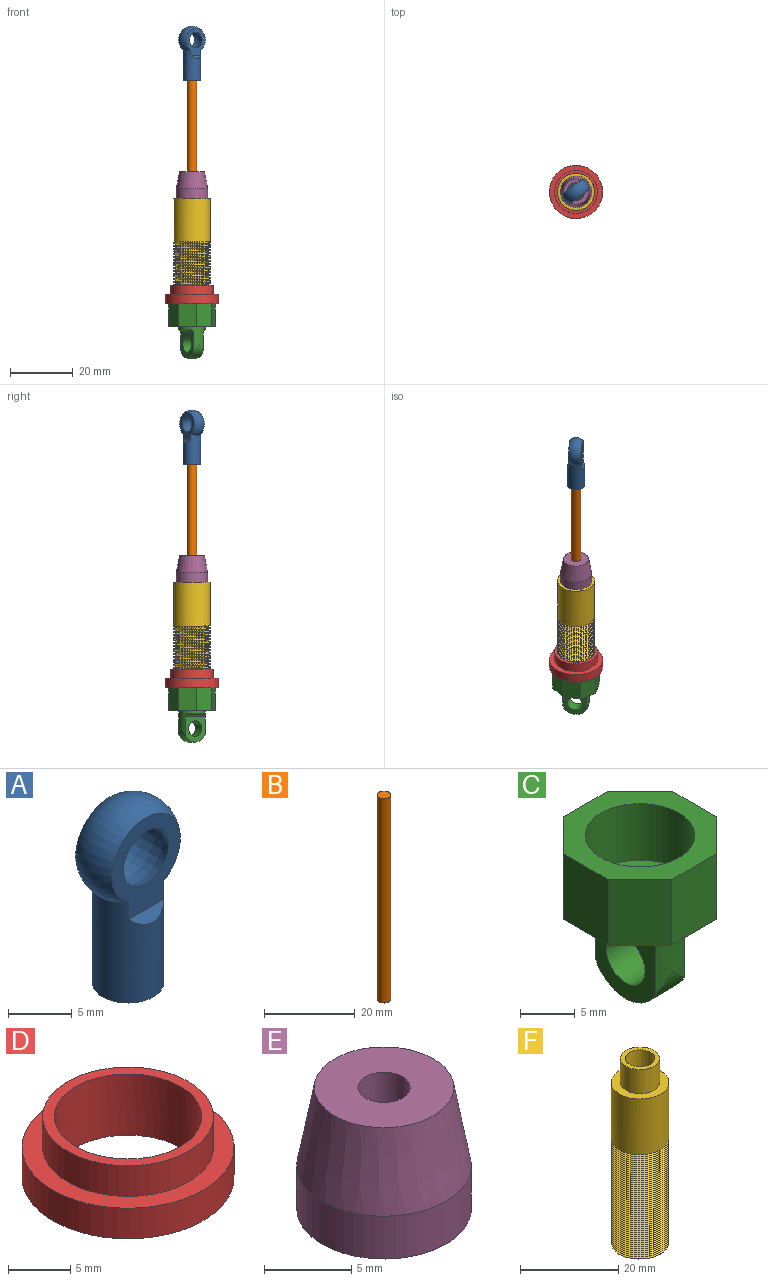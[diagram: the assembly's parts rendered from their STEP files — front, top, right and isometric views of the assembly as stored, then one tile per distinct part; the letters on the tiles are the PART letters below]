
ASSEMBLY  parts=6 mates=9
PART A: 10 faces, bbox 7.6x5.6x16.8 mm
  f0: cylinder r=2.8mm len=9.75mm, axis (0,0,1), area 150.2mm2, adj f1,f2,f3,f5,f8,f9
  f1: plane 8.79x7.59mm, normal (0,-1,0), area 31mm2, adj f0,f2,f4,f8
  f2: torus R=1.32mm, axis (0,1,0), area 92.4mm2, adj f0,f1,f3
  f3: plane 8.79x7.59mm, normal (0,1,0), area 31mm2, adj f0,f2,f4,f9
  f4: revolved ~6x6mm, area 74.1mm2, adj f1,f3
  f5: plane 5.6x5.6mm, normal (0,0,-1), area 17.6mm2, adj f0,f7
  f6: torus R=1.32mm, axis (0,1,0), area 7.4mm2, adj f7
  f7: cylinder r=1.5mm len=8.88mm, axis (0,0,-1), area 83.1mm2, adj f5,f6
  f8: plane 3.92x0.8mm, normal (0,-0.71,0.71), area 3.1mm2, adj f0,f1
  f9: plane 3.92x0.8mm, normal (0,0.71,0.71), area 3.1mm2, adj f0,f3
PART B: 3 faces, bbox 3x3x55 mm
  f0: cylinder r=1.5mm len=55mm, axis (0,0,-1), area 518.4mm2, adj f1,f2
  f1: plane 3x3mm, normal (0,0,1), area 7.1mm2, adj f0
  f2: plane 3x3mm, normal (0,0,-1), area 7.1mm2, adj f0
PART C: 21 faces, bbox 14x14x17.3 mm
  f0: cylinder r=4.25mm len=8.5mm, axis (0,0,1), area 71.3mm2, adj f1,f2,f12,f15,f16,f18,f19,f20
  f1: plane 8x7.65mm, normal (1,0,0), area 36.4mm2, adj f0,f17,f18,f19
  f2: plane 8x7.65mm, normal (-1,0,0), area 36.4mm2, adj f0,f17,f18,f20
  f3: plane 7.3x5.8mm, normal (0,-1,0), area 42.3mm2, adj f4,f10,f11,f12
  f4: plane 7.3x4.1mm, normal (0.71,-0.71,0), area 42.3mm2, adj f3,f5,f11,f12
  f5: plane 7.3x5.8mm, normal (1,0,0), area 42.3mm2, adj f4,f6,f11,f12
  f6: plane 7.3x4.1mm, normal (0.71,0.71,0), area 42.3mm2, adj f5,f7,f11,f12
  f7: plane 7.3x5.8mm, normal (0,1,0), area 42.3mm2, adj f6,f8,f11,f12
  f8: plane 7.3x4.1mm, normal (-0.71,0.71,0), area 42.3mm2, adj f7,f9,f11,f12
  f9: plane 7.3x5.8mm, normal (-1,0,0), area 42.3mm2, adj f8,f10,f11,f12
  f10: plane 7.3x4.1mm, normal (-0.71,-0.71,0), area 42.3mm2, adj f3,f9,f11,f12
  f11: plane 14x14mm, normal (0,0,1), area 83.8mm2, adj f3,f4,f5,f6,f7,f8,f9,f10
  f12: plane 14x14mm, normal (0,0,-1), area 105.6mm2, adj f0,f3,f4,f5,f6,f7,f8,f9
  f13: cylinder r=5mm len=10mm, axis (0,0,1), area 197.9mm2, adj f11,f14
  f14: plane 10x10mm, normal (0,0,1), area 78.5mm2, adj f13
  f15: plane 6.31x1.4mm, normal (0,0,-1), area 6.1mm2, adj f0,f19
  f16: plane 6.31x1.4mm, normal (0,0,-1), area 6.1mm2, adj f0,f20
  f17: cylinder r=2.5mm len=5mm, axis (-1,0,0), area 58.1mm2, adj f1,f2
  f18: cylinder r=4.25mm len=8.5mm, axis (-1,0,0), area 42.4mm2, adj f0,f1,f2
  f19: cylinder r=1mm len=7.65mm, axis (0,1,0), area 11.3mm2, adj f0,f1,f15
  f20: cylinder r=1mm len=7.65mm, axis (0,-1,0), area 11.3mm2, adj f0,f2,f16
PART D: 6 faces, bbox 17x17x6 mm
  f0: cylinder r=8.5mm len=17mm, axis (0,0,-1), area 160.2mm2, adj f1,f2
  f1: plane 17x17mm, normal (0,0,1), area 79.6mm2, adj f0,f3
  f2: plane 17x17mm, normal (0,0,-1), area 117.6mm2, adj f0,f5
  f3: cylinder r=6.85mm len=13.7mm, axis (0,0,-1), area 129.1mm2, adj f1,f4
  f4: plane 13.7x13.7mm, normal (0,0,1), area 38.1mm2, adj f3,f5
  f5: cylinder r=5.9mm len=11.8mm, axis (0,0,-1), area 222.4mm2, adj f2,f4
PART E: 7 faces, bbox 10x10x8.5 mm
  f0: cylinder r=5mm len=10mm, axis (0,0,-1), area 94.2mm2, adj f1,f3
  f1: plane 10x10mm, normal (0,0,-1), area 28.3mm2, adj f0,f4
  f2: plane 8x8mm, normal (0,0,1), area 43.2mm2, adj f3,f6
  f3: cone r=5mm half-angle=10.3deg, axis (0,0,-1), area 158.1mm2, adj f0,f2
  f4: cylinder r=4mm len=8mm, axis (0,0,-1), area 150.8mm2, adj f1,f5
  f5: plane 8x8mm, normal (0,0,-1), area 43.2mm2, adj f4,f6
  f6: cylinder r=1.5mm len=3mm, axis (0,0,-1), area 23.6mm2, adj f2,f5
PART F: 66 faces, bbox 12.2x14.1x46.7 mm
  f0: cylinder r=5.9mm len=14.26mm, axis (0,0,-1), area 519.2mm2, adj f52,f53,f63,f64
  f1: cylinder r=5.9mm len=11.8mm, axis (0,0,-1), area 0.2mm2, adj f2,f54,f62,f65
  f2: cylinder r=5.9mm len=11.8mm, axis (0,0,-1), area 0.5mm2, adj f1,f3,f62,f64
  f3: cylinder r=5.9mm len=11.8mm, axis (0,0,-1), area 0.5mm2, adj f2,f4,f62,f64
  f4: cylinder r=5.9mm len=11.8mm, axis (0,0,-1), area 0.5mm2, adj f3,f5,f62,f64
  f5: cylinder r=5.9mm len=11.8mm, axis (0,0,-1), area 0.5mm2, adj f4,f6,f62,f64
  f6: cylinder r=5.9mm len=11.8mm, axis (0,0,-1), area 0.5mm2, adj f5,f7,f62,f64
  f7: cylinder r=5.9mm len=11.8mm, axis (0,0,-1), area 0.5mm2, adj f6,f8,f62,f64
  f8: cylinder r=5.9mm len=11.8mm, axis (0,0,-1), area 0.5mm2, adj f7,f9,f62,f64
  f9: cylinder r=5.9mm len=11.8mm, axis (0,0,-1), area 0.5mm2, adj f8,f10,f62,f64
  f10: cylinder r=5.9mm len=11.8mm, axis (0,0,-1), area 0.5mm2, adj f9,f11,f62,f64
  f11: cylinder r=5.9mm len=11.8mm, axis (0,0,-1), area 0.5mm2, adj f10,f12,f62,f64
  f12: cylinder r=5.9mm len=11.8mm, axis (0,0,-1), area 0.5mm2, adj f11,f13,f62,f64
  f13: cylinder r=5.9mm len=11.8mm, axis (0,0,-1), area 0.5mm2, adj f12,f14,f62,f64
  f14: cylinder r=5.9mm len=11.8mm, axis (0,0,-1), area 0.5mm2, adj f13,f15,f62,f64
  f15: cylinder r=5.9mm len=11.8mm, axis (0,0,-1), area 0.5mm2, adj f14,f16,f62,f64
  f16: cylinder r=5.9mm len=11.8mm, axis (0,0,-1), area 0.5mm2, adj f15,f17,f62,f64
  f17: cylinder r=5.9mm len=11.8mm, axis (0,0,-1), area 0.5mm2, adj f16,f18,f62,f64
  f18: cylinder r=5.9mm len=11.8mm, axis (0,0,-1), area 0.5mm2, adj f17,f19,f62,f64
  f19: cylinder r=5.9mm len=11.8mm, axis (0,0,-1), area 0.5mm2, adj f18,f20,f62,f64
  f20: cylinder r=5.9mm len=11.8mm, axis (0,0,-1), area 0.5mm2, adj f19,f21,f62,f64
  f21: cylinder r=5.9mm len=11.8mm, axis (0,0,-1), area 0.5mm2, adj f20,f22,f62,f64
  f22: cylinder r=5.9mm len=11.8mm, axis (0,0,-1), area 0.5mm2, adj f21,f23,f62,f64
  f23: cylinder r=5.9mm len=11.8mm, axis (0,0,-1), area 0.5mm2, adj f22,f24,f62,f64
  f24: cylinder r=5.9mm len=11.8mm, axis (0,0,-1), area 0.5mm2, adj f23,f25,f62,f64
  f25: cylinder r=5.9mm len=11.8mm, axis (0,0,-1), area 0.5mm2, adj f24,f26,f62,f64
  f26: cylinder r=5.9mm len=11.8mm, axis (0,0,-1), area 0.5mm2, adj f25,f27,f62,f64
  f27: cylinder r=5.9mm len=11.8mm, axis (0,0,-1), area 0.5mm2, adj f26,f28,f62,f64
  f28: cylinder r=5.9mm len=11.8mm, axis (0,0,-1), area 0.5mm2, adj f27,f29,f62,f64
  f29: cylinder r=5.9mm len=11.8mm, axis (0,0,-1), area 0.5mm2, adj f28,f30,f62,f64
  f30: cylinder r=5.9mm len=11.8mm, axis (0,0,-1), area 0.5mm2, adj f29,f31,f62,f64
  f31: cylinder r=5.9mm len=11.8mm, axis (0,0,-1), area 0.5mm2, adj f30,f32,f62,f64
  f32: cylinder r=5.9mm len=11.8mm, axis (0,0,-1), area 0.5mm2, adj f31,f33,f62,f64
  f33: cylinder r=5.9mm len=11.8mm, axis (0,0,-1), area 0.5mm2, adj f32,f34,f62,f64
  f34: cylinder r=5.9mm len=11.8mm, axis (0,0,-1), area 0.5mm2, adj f33,f35,f62,f64
  f35: cylinder r=5.9mm len=11.8mm, axis (0,0,-1), area 0.5mm2, adj f34,f36,f62,f64
  f36: cylinder r=5.9mm len=11.8mm, axis (0,0,-1), area 0.5mm2, adj f35,f37,f62,f64
  f37: cylinder r=5.9mm len=11.8mm, axis (0,0,-1), area 0.5mm2, adj f36,f38,f62,f64
  f38: cylinder r=5.9mm len=11.8mm, axis (0,0,-1), area 0.5mm2, adj f37,f39,f62,f64
  f39: cylinder r=5.9mm len=11.8mm, axis (0,0,-1), area 0.5mm2, adj f38,f40,f62,f64
  f40: cylinder r=5.9mm len=11.8mm, axis (0,0,-1), area 0.5mm2, adj f39,f41,f62,f64
  f41: cylinder r=5.9mm len=11.8mm, axis (0,0,-1), area 0.5mm2, adj f40,f42,f62,f64
  f42: cylinder r=5.9mm len=11.8mm, axis (0,0,-1), area 0.5mm2, adj f41,f43,f62,f64
  f43: cylinder r=5.9mm len=11.8mm, axis (0,0,-1), area 0.5mm2, adj f42,f44,f62,f64
  f44: cylinder r=5.9mm len=11.8mm, axis (0,0,-1), area 0.5mm2, adj f43,f45,f62,f64
  f45: cylinder r=5.9mm len=11.8mm, axis (0,0,-1), area 0.5mm2, adj f44,f46,f62,f64
  f46: cylinder r=5.9mm len=11.8mm, axis (0,0,-1), area 0.5mm2, adj f45,f47,f62,f64
  f47: cylinder r=5.9mm len=11.8mm, axis (0,0,-1), area 0.5mm2, adj f46,f48,f62,f64
  f48: cylinder r=5.9mm len=11.8mm, axis (0,0,-1), area 0.5mm2, adj f47,f49,f62,f64
  f49: cylinder r=5.9mm len=11.8mm, axis (0,0,-1), area 0.5mm2, adj f48,f50,f62,f64
  f50: cylinder r=5.9mm len=11.8mm, axis (0,0,-1), area 0.5mm2, adj f49,f51,f62,f64
  f51: cylinder r=5.9mm len=11.8mm, axis (0,0,-1), area 0.5mm2, adj f50,f52,f62,f64
  f52: cylinder r=5.9mm len=11.8mm, axis (0,0,-1), area 0.5mm2, adj f0,f51,f62,f64
  f53: plane 11.8x11.8mm, normal (0,0,1), area 59.1mm2, adj f0,f55
  f54: plane 11.77x11.75mm, normal (0,0,-1), area 22mm2, adj f1,f61,f62,f65
  f55: cylinder r=4mm len=8mm, axis (0,0,-1), area 150.8mm2, adj f53,f56
  f56: plane 8x8mm, normal (0,0,1), area 22mm2, adj f55,f57
  f57: cylinder r=3mm len=6mm, axis (0,0,1), area 94.2mm2, adj f56,f58
  f58: plane 6x6mm, normal (0,0,1), area 21.2mm2, adj f57,f59
  f59: cylinder r=1.5mm len=3mm, axis (0,0,1), area 18.8mm2, adj f58,f60
  f60: plane 10x10mm, normal (0,0,-1), area 71.5mm2, adj f59,f61
  f61: cylinder r=5mm len=39mm, axis (0,0,-1), area 1225.2mm2, adj f54,f60
  f62: bspline ~26.24x13.63mm, area 1013.4mm2, adj f1,f2,f3,f4,f5,f6,f7,f8
  f63: plane 0.5x0.49mm, normal (0,-1,0), area 0.1mm2, adj f0,f62,f64
  f64: bspline ~26.24x13.63mm, area 1026.9mm2, adj f0,f2,f3,f4,f5,f6,f7,f8
  f65: bspline ~11.8x6.81mm, area 4.9mm2, adj f1,f54,f64
PLACE A rot(axis=(0,0,-1),142.5deg) t=(-8.59,-7.15,82.07)mm
PLACE B rot(axis=(0,0,-1),167.9deg) t=(-9.81,-5.56,22.57)mm
PLACE C rot(axis=(0,0,-1),146.9deg) t=(-9.81,-5.56,-9.43)mm
PLACE D rot(axis=(0,0,-1),75.6deg) t=(-9.81,-5.56,-2.13)mm
PLACE E rot(axis=(0,0,1),127.5deg) t=(-9.81,-5.56,31.57)mm
PLACE F t=(-9.81,-5.56,-8.43)mm fixed
MATE cylindrical C.f13 <-> F.f0  axis (0,0,1) through (-9.81,-5.56,-2.13)mm
MATE planar C.f13 <-> F.f54  axis (0,0,1) through (-9.81,-5.56,-8.43)mm
MATE cylindrical D.f5 <-> F.f0  axis (0,0,-1) through (-9.81,-5.56,-2.13)mm
MATE slider A.f0 <-> E.f0  axis (0,0,1) through (-9.81,-5.56,69.07)mm
MATE cylindrical A.f0 <-> F.f55  axis (0,0,1) through (-9.81,-5.56,73.97)mm
MATE cylindrical B.f0 <-> A.f0  axis (0,0,-1) through (-9.81,-5.56,50.07)mm
MATE cylindrical E.f0 <-> F.f55  axis (0,0,-1) through (-9.81,-5.56,33.07)mm
MATE planar D.f0 <-> C.f13  axis (0,0,-1) through (-9.81,-5.56,-2.13)mm
MATE planar E.f0 <-> F.f0  axis (0,0,-1) through (-9.81,-5.56,31.57)mm
